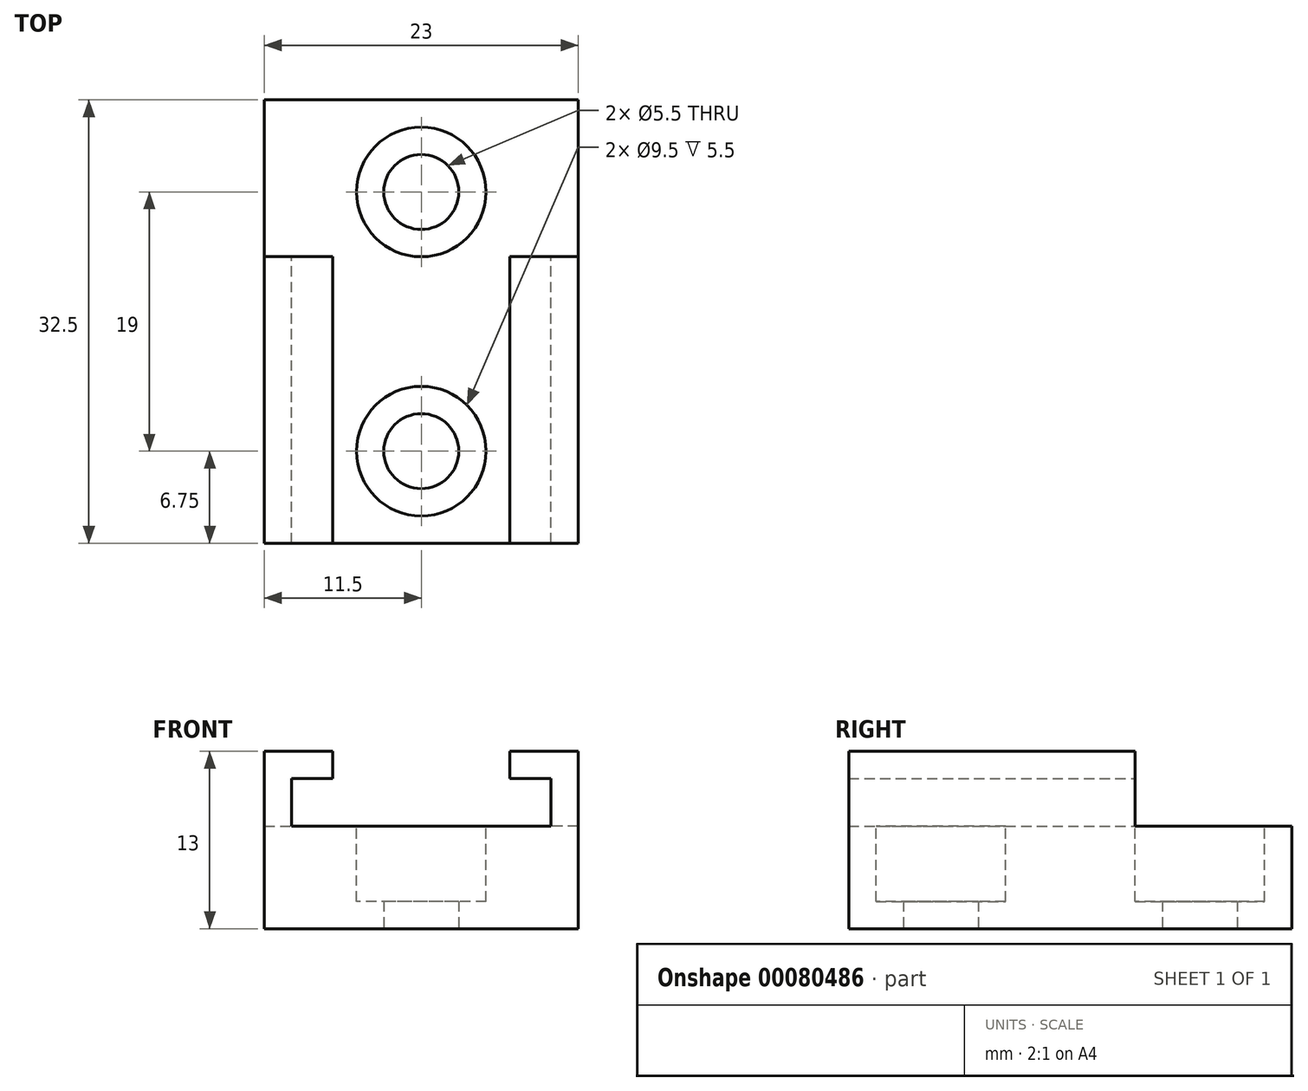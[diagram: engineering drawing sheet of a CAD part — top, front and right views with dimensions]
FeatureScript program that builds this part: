
annotation { "Feature Type Name" : "Feature", "Feature Type Description" : "" }
export const myFeature = defineFeature(function(context is Context, id is Id, definition is map)
    precondition{}
    {
        {
            var Q0;
            Q0=qCreatedBy(makeId("Top.planeOp"),FACE);
            var sketch = newSketch(context, id + "F0", { "sketchPlane" : qUnion([Q0])});
            skLineSegment(sketch, "E0.bottom", {"start": v(11.5, 16.25) * mm, "end": v(-11.5, 16.25) * mm});
            skLineSegment(sketch, "E0.top", {"start": v(11.5, -16.25) * mm, "end": v(-11.5, -16.25) * mm});
            skLineSegment(sketch, "E0.left", {"start": v(11.5, 16.25) * mm, "end": v(11.5, -16.25) * mm});
            skLineSegment(sketch, "E0.right", {"start": v(-11.5, 16.25) * mm, "end": v(-11.5, -16.25) * mm});
            skPoint(sketch, "E0.middle", {"position": v(0, 0) * mm});
            skLineSegment(sketch, "E1", {"start": v(-11.5, 0) * mm, "end": v(11.5, 0) * mm, "construction": true});
            skLineSegment(sketch, "E2", {"start": v(0, -9.5) * mm, "end": v(0, 9.5) * mm, "construction": true});
            skCircle(sketch, "E3", {"center": v(0, 9.5) * mm, "radius": 2.75 * mm});
            skCircle(sketch, "E4.MirrorC", {"center": v(0, -9.5) * mm, "radius": 2.75 * mm});
            skSolve(sketch);
        }
        {
            var Q0;
            Q0 = qSketchRegion(id + "F0", true);
            extrude(context, id + "F1", {"entities" : qUnion([Q0]), "depth" : 7.5 * mm});
        }
        {
            var Q0;
            Q0=makeQuery(id+"F1.opExtrude","CAP_FACE",FACE,{"disambiguationData":[OSD([sQuery(id+"F0.wireOp",EDGE,"E0.bottom"),sQuery(id+"F0.wireOp",EDGE,"E0.top"),sQuery(id+"F0.wireOp",EDGE,"E0.left"),sQuery(id+"F0.wireOp",EDGE,"E0.right"),sQuery(id+"F0.wireOp",EDGE,"E3"),sQuery(id+"F0.wireOp",EDGE,"E4.MirrorC")])],"isStart":false});
            var sketch = newSketch(context, id + "F2", { "sketchPlane" : qUnion([Q0])});
            skCircle(sketch, "E5", {"center": v(0, -9.5) * mm, "radius": 4.75 * mm});
            skCircle(sketch, "E6", {"center": v(0, 9.5) * mm, "radius": 4.75 * mm});
            skSolve(sketch);
        }
        {
            var Q0;
            Q0 = qSketchRegion(id + "F2", true);
            extrude(context, id + "F3", {"entities" : qUnion([Q0]), "operationType" : NewBodyOperationType.REMOVE, "oppositeDirection" : true, "depth" : 5.5 * mm});
        }
        {
            var Q0;
            Q0=makeQuery(id+"F1.opExtrude","CAP_FACE",FACE,{"disambiguationData":[OSD([sQuery(id+"F0.wireOp",EDGE,"E0.bottom"),sQuery(id+"F0.wireOp",EDGE,"E0.top"),sQuery(id+"F0.wireOp",EDGE,"E0.left"),sQuery(id+"F0.wireOp",EDGE,"E0.right"),sQuery(id+"F0.wireOp",EDGE,"E3"),sQuery(id+"F0.wireOp",EDGE,"E4.MirrorC")])],"isStart":false});
            var sketch = newSketch(context, id + "F4", { "sketchPlane" : qUnion([Q0])});
            skLineSegment(sketch, "E7", {"start": v(0, 16.25) * mm, "end": v(0, -16.25) * mm, "construction": true});
            skLineSegment(sketch, "E8.bottom", {"start": v(-11.5, -16.25) * mm, "end": v(-9.5, -16.25) * mm});
            skLineSegment(sketch, "E8.top", {"start": v(-11.5, 4.75) * mm, "end": v(-9.5, 4.75) * mm});
            skLineSegment(sketch, "E8.left", {"start": v(-11.5, -16.25) * mm, "end": v(-11.5, 4.75) * mm});
            skLineSegment(sketch, "E8.right", {"start": v(-9.5, -16.25) * mm, "end": v(-9.5, 4.75) * mm});
            skLineSegment(sketch, "E9.MirrorCS", {"start": v(11.5, 4.75) * mm, "end": v(9.5, 4.75) * mm});
            skLineSegment(sketch, "E10.MirrorCS", {"start": v(9.5, -16.25) * mm, "end": v(9.5, 4.75) * mm});
            skLineSegment(sketch, "E11.MirrorCS", {"start": v(11.5, -16.25) * mm, "end": v(11.5, 4.75) * mm});
            skLineSegment(sketch, "E12.MirrorCS", {"start": v(11.5, -16.25) * mm, "end": v(9.5, -16.25) * mm});
            skSolve(sketch);
        }
        {
            var Q0;
            Q0 = qSketchRegion(id + "F4", true);
            extrude(context, id + "F5", {"entities" : qUnion([Q0]), "operationType" : NewBodyOperationType.ADD, "depth" : 3.5 * mm});
        }
        {
            var Q0;
            Q0=makeQuery(id+"F5.opExtrude","CAP_FACE",FACE,{"disambiguationData":[OSD([sQuery(id+"F4.wireOp",EDGE,"E8.bottom"),sQuery(id+"F4.wireOp",EDGE,"E8.top"),sQuery(id+"F4.wireOp",EDGE,"E8.left"),sQuery(id+"F4.wireOp",EDGE,"E8.right")])],"isStart":false});
            var sketch = newSketch(context, id + "F6", { "sketchPlane" : qUnion([Q0])});
            skLineSegment(sketch, "E13.bottom", {"start": v(-11.5, -16.25) * mm, "end": v(-6.5, -16.25) * mm});
            skLineSegment(sketch, "E13.top", {"start": v(-11.5, 4.75) * mm, "end": v(-6.5, 4.75) * mm});
            skLineSegment(sketch, "E13.left", {"start": v(-11.5, -16.25) * mm, "end": v(-11.5, 4.75) * mm});
            skLineSegment(sketch, "E13.right", {"start": v(-6.5, -16.25) * mm, "end": v(-6.5, 4.75) * mm});
            skLineSegment(sketch, "E14", {"start": v(0, 0) * mm, "end": v(0, -19.72) * mm, "construction": true});
            skLineSegment(sketch, "E15.MirrorCS", {"start": v(6.5, -16.25) * mm, "end": v(6.5, 4.75) * mm});
            skLineSegment(sketch, "E16.MirrorCS", {"start": v(11.5, 4.75) * mm, "end": v(6.5, 4.75) * mm});
            skLineSegment(sketch, "E17.MirrorCS", {"start": v(11.5, -16.25) * mm, "end": v(11.5, 4.75) * mm});
            skLineSegment(sketch, "E18.MirrorCS", {"start": v(11.5, -16.25) * mm, "end": v(6.5, -16.25) * mm});
            skSolve(sketch);
        }
        {
            var Q0;
            Q0 = qSketchRegion(id + "F6", true);
            extrude(context, id + "F7", {"entities" : qUnion([Q0]), "operationType" : NewBodyOperationType.ADD, "depth" : 2 * mm});
        }
    });
